# Revit family: IS_Tesi_T3520_BIM_GB
name_source: partatom
category: Plumbing Fixtures
revit_build: Autodesk Revit MEP 2012 (Build: 20110309_2315(x64)
units: mm (PartAtom-declared; Revit-internal decimal feet)

## types (1)
- T352001-Tesi Semipedestal SMALL
    Accessories = www.idealspec.co.uk
    AreaUnits = millimeters
    Assembly Code = C1030200
    AssetType = Fixed
    BIMObjectName = ISI_IdealStandard_PedestalWashBasins_Tesi-SmallSemiPed_T3520
    BarCode = 8014140430254
    Brand = Ideal Standard
    CWFU = 0
    Color = White
    ConnectionType = Plumbing
    Cost = 0 $
    Default Elevation = 800 mm  [stored 2.62467 ft]
    Description = Tesi small semi-pedestal
    DrainSize = 0 mm  [stored 0 ft]
    DurationUnit = year
    ECA = No
    ExpectedLife = 30
    Features = small semi-pedestal
    Finish = White
    HWFU = 0
    IfcExportAs = IfcSanitaryType
    IfcExportType = SEMIPEDESTAL
    InstallationInstructions = www.idealspec.co.uk/resources.html
    LinearUnits = millimeters
    ManufacturerURL = www.idealspec.co.uk
    Material = Vitreous china
    Model = T352001
    ModelNumber = T352001
    ModelReference = Tesi small semi-pedestal
    NBSDescription = Pedestal wash basins
    NBSReference = 45-35-70/365
    Name = PedestalWashBasins_Tesi-SmallSemiPed_T3520_IdealStandard
    NettWeight = 6.1 Kg
    NominalDepth = 263 mm
    NominalHeight = 340 mm
    NominalLength = 263 mm
    NominalWidth = 175 mm
    ProductInformation = www.idealspec.co.uk/assets/datasheet/T352001
    Shape = Sculptured
    Size = 175 x 263 x 340 mm
    Space = Internal
    URL = www.idealspec.co.uk
    Uniclass2 = Pr_40_20_96_63
    Version = 1
    VolumeUnits = Litres
    WFU = 0
    WRAS = No
    WarrantyDescription = Manufacturers Warranty
    WarrantyDurationParts = 99
    WarrantyDurationUnit = year
    WashHandBasinMounting = Pedestal
    WashHandBasinType = Hand Rinse
    WaterEfficientProduct = No

note: [stored X ft] marks values corroborated as IEEE doubles in the binary element streams (Revit-internal decimal feet)

## geometry (parser evidence)
native form markers: Sweep x3
no freeform markers — native parametric forms only
